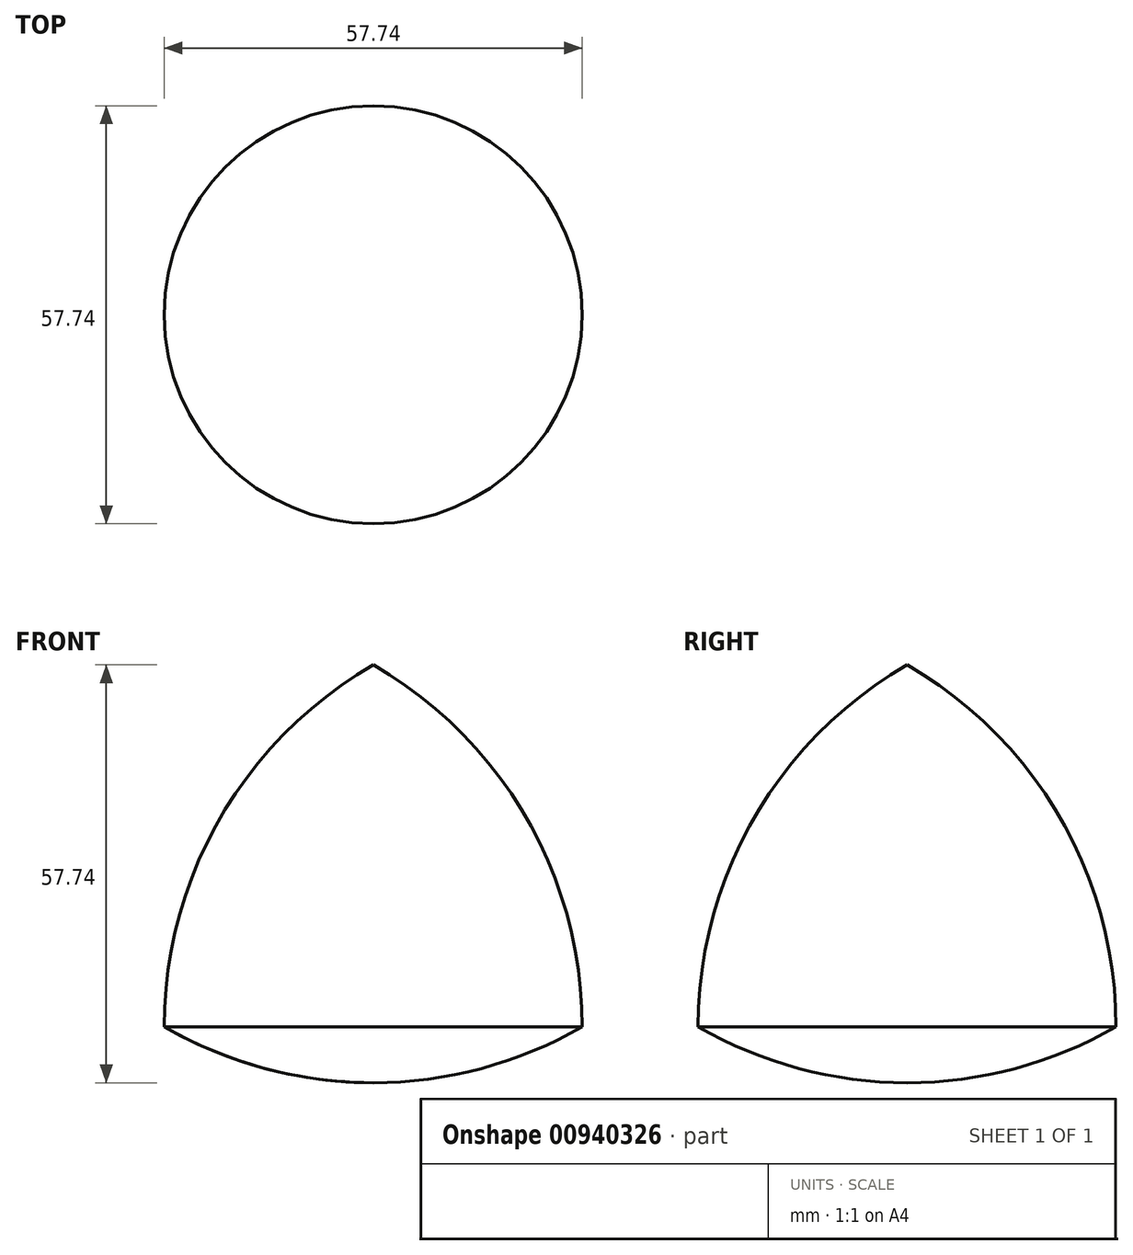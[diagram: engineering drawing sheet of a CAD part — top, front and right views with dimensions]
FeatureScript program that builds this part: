
annotation { "Feature Type Name" : "Feature", "Feature Type Description" : "" }
export const myFeature = defineFeature(function(context is Context, id is Id, definition is map)
    precondition{}
    {
        {
            var Q0;
            Q0=qCreatedBy(makeId("Front.planeOp"),FACE);
            var sketch = newSketch(context, id + "F0", { "sketchPlane" : qUnion([Q0])});
            skLineSegment(sketch, "E0", {"start": v(0, 50) * mm, "end": v(28.87, 0) * mm, "construction": true});
            skLineSegment(sketch, "E1", {"start": v(28.87, 0) * mm, "end": v(0, 0) * mm, "construction": true});
            skArc(sketch, "E2", {"start": v(0, -7.74) * mm, "mid": v(14.94, -5.77) * mm, "end": v(28.87, 0) * mm});
            skArc(sketch, "E3", {"start": v(28.87, 0) * mm, "mid": v(21.13, 28.87) * mm, "end": v(0, 50) * mm});
            skLineSegment(sketch, "E4", {"start": v(0, 50) * mm, "end": v(0, -7.74) * mm});
            skSolve(sketch);
        }
        {
            var Q0;
            Q0=makeQuery(id+"F0.imprint","IMPRINT",FACE,{"disambiguationData":[TD([[makeQuery(id+"F0.imprint","IMPRINT",EDGE,{"derivedFrom":sQuery(id+"F0.wireOp",EDGE,"E2")}),1.0]])]});
            var Q1;
            Q1=sQuery(id+"F0.wireOp",EDGE,"EzLlge5y-Fmzd-flZw-3K7L-40YKhNg5V14F");
            var Q2;
            Q2=sQuery(id+"F0.wireOp",EDGE,"xHnhE9OP-sqHD-6MuT-sXbD-zQb9gdvg0NqE");
            var Q3;
            Q3=sQuery(id+"F0.wireOp",EDGE,"jbeIay0O-oHlM-lQWC-zueF-GVeJ507ir1Zk");
            var Q4;
            Q4=sQuery(id+"F0.wireOp",EDGE,"E4");
            revolve(context, id + "F1", {"surfaceOperationType" : NewSurfaceOperationType.NEW, "entities" : qUnion([Q0]), "surfaceEntities" : qUnion([Q1, Q2, Q3]), "axis" : qUnion([Q4]), "revolveType" : RevolveType.FULL});
        }
    });
